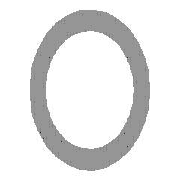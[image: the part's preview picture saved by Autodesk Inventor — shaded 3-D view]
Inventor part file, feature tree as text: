
AUTODESK INVENTOR PART (.ipt)
format: ipt  version: 2021 (Build 250183000, 183)  size: 115,200 bytes
history: native  units: mm (DEFAULTED — no unit token found)
features: other x4, sketch x3, extrude x1, plane x1
ambient origin geometry x8: Origin, YZ Plane, XZ Plane, XY Plane, X Axis, Y Axis, Z Axis, Center Point
bodies: Solid1 (feature_tree)
feature tree (9):
  parser-record x1  (decoder bookkeeping rows leaked as tree rows — omitted from the tree; the rows remain in map.json)
  other  "Driven Length"
  other  "Plano inicial"
  other  "Plano final"
  extrude  "Cuerpo"  Depth=3.556mm
  sketch  "Boceto"  dims[d4=-0.0mm d5=150.0mm d6=90.0deg d7=150.0mm]
  sketch  "Sketch3"  dims[d0=42.164mm d1=3.556mm]
  plane  "Work Plane3"
  sketch  "Sketch4"  dims[d2=150.0mm d3=0.0mm]
